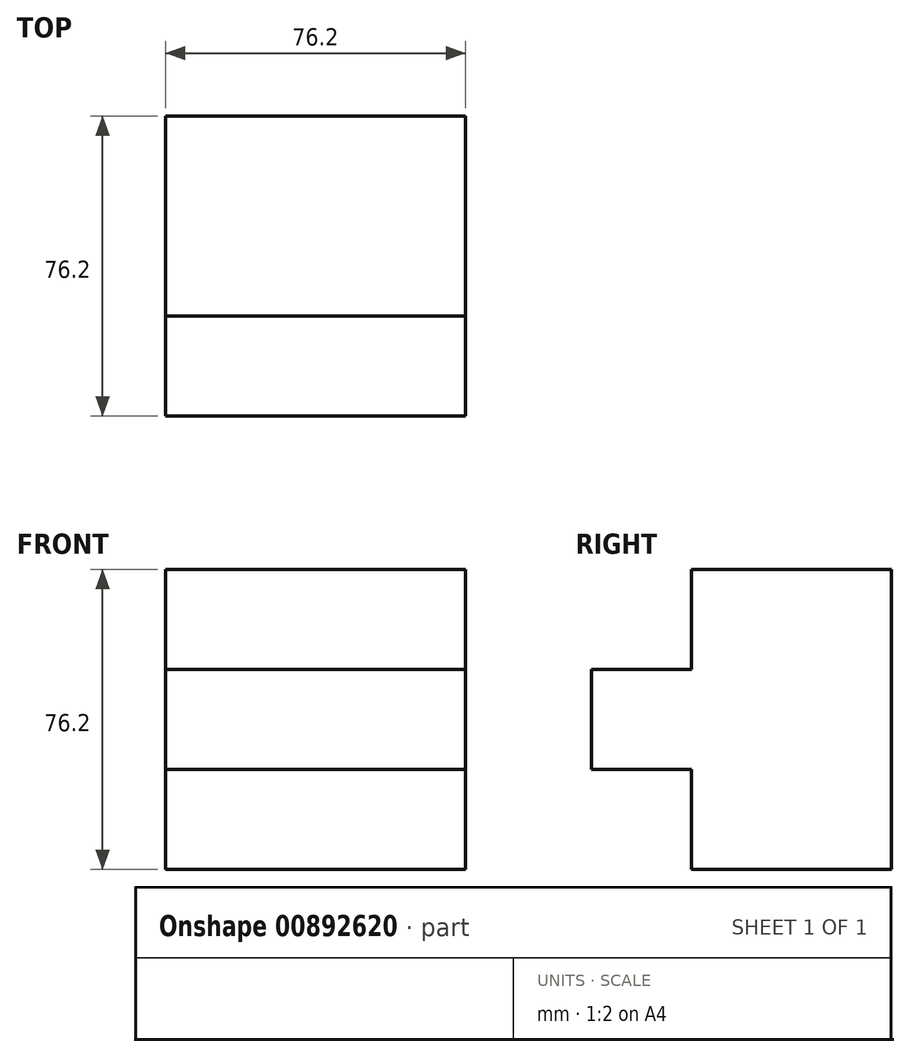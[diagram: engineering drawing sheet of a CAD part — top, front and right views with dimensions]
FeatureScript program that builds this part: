
annotation { "Feature Type Name" : "Feature", "Feature Type Description" : "" }
export const myFeature = defineFeature(function(context is Context, id is Id, definition is map)
    precondition{}
    {
        {
            var Q0;
            Q0=qCreatedBy(makeId("Front.planeOp"),FACE);
            var sketch = newSketch(context, id + "F0", { "sketchPlane" : qUnion([Q0])});
            skLineSegment(sketch, "E0.bottom", {"start": v(-111.53, 102.45) * mm, "end": v(-35.33, 102.45) * mm});
            skLineSegment(sketch, "E0.top", {"start": v(-111.53, 26.25) * mm, "end": v(-35.33, 26.25) * mm});
            skLineSegment(sketch, "E0.left", {"start": v(-111.53, 102.45) * mm, "end": v(-111.53, 26.25) * mm});
            skLineSegment(sketch, "E0.right", {"start": v(-35.33, 102.45) * mm, "end": v(-35.33, 26.25) * mm});
            skSolve(sketch);
        }
        {
            var Q0;
            Q0=makeQuery(id+"F0.imprint","IMPRINT",FACE,{"disambiguationData":[TD([[makeQuery(id+"F0.imprint","IMPRINT",EDGE,{"derivedFrom":sQuery(id+"F0.wireOp",EDGE,"E0.bottom")}),-1.0]])]});
            extrude(context, id + "F1", {"entities" : qUnion([Q0]), "depth" : 50.8 * mm, "offsetDistance" : 25.4 * mm});
        }
        {
            var Q0;
            Q0=makeQuery(id+"F1.opExtrude","CAP_FACE",FACE,{"disambiguationData":[OSD([sQuery(id+"F0.wireOp",EDGE,"E0.bottom"),sQuery(id+"F0.wireOp",EDGE,"E0.top"),sQuery(id+"F0.wireOp",EDGE,"E0.left"),sQuery(id+"F0.wireOp",EDGE,"E0.right")])],"isStart":false});
            var sketch = newSketch(context, id + "F2", { "sketchPlane" : qUnion([Q0])});
            skLineSegment(sketch, "E1", {"start": v(-111.53, 26.25) * mm, "end": v(-111.53, 51.65) * mm, "construction": true});
            skLineSegment(sketch, "E2", {"start": v(-111.53, 51.65) * mm, "end": v(-35.33, 51.65) * mm});
            skLineSegment(sketch, "E3", {"start": v(-35.33, 51.65) * mm, "end": v(-35.33, 77.05) * mm});
            skLineSegment(sketch, "E4", {"start": v(-35.33, 77.05) * mm, "end": v(-111.53, 77.05) * mm});
            skLineSegment(sketch, "E5", {"start": v(-111.53, 77.05) * mm, "end": v(-111.53, 51.65) * mm});
            skSolve(sketch);
        }
        {
            var Q0;
            Q0=makeQuery(id+"F2.imprint","IMPRINT",FACE,{"disambiguationData":[TD([[makeQuery(id+"F2.imprint","IMPRINT",EDGE,{"derivedFrom":sQuery(id+"F2.wireOp",EDGE,"E2")}),1.0]])]});
            extrude(context, id + "F3", {"entities" : qUnion([Q0]), "operationType" : NewBodyOperationType.ADD, "depth" : 25.4 * mm, "offsetDistance" : 25.4 * mm});
        }
    });
